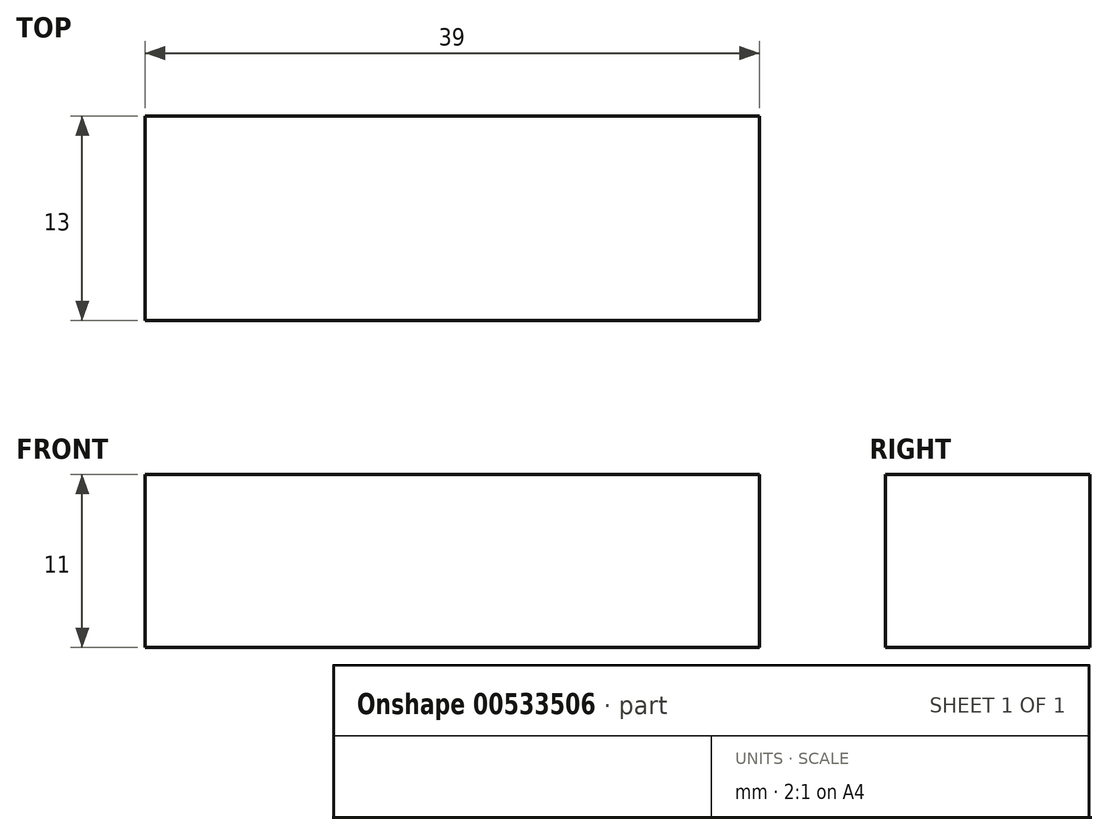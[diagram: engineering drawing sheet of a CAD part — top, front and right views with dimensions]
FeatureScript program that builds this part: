
annotation { "Feature Type Name" : "Feature", "Feature Type Description" : "" }
export const myFeature = defineFeature(function(context is Context, id is Id, definition is map)
    precondition{}
    {
        {
            var Q0;
            Q0=qCreatedBy(makeId("Top.planeOp"),FACE);
            var sketch = newSketch(context, id + "F0", { "sketchPlane" : qUnion([Q0])});
            skLineSegment(sketch, "E0.bottom", {"start": v(0, 0) * mm, "end": v(39, 0) * mm});
            skLineSegment(sketch, "E0.top", {"start": v(0, 13) * mm, "end": v(39, 13) * mm});
            skLineSegment(sketch, "E0.left", {"start": v(0, 0) * mm, "end": v(0, 13) * mm});
            skLineSegment(sketch, "E0.right", {"start": v(39, 0) * mm, "end": v(39, 13) * mm});
            skSolve(sketch);
        }
        {
            var Q0;
            Q0=qSketchRegion(id+"F0",true);
            extrude(context, id + "F1", {"entities" : qUnion([Q0]), "depth" : 11 * mm, "offsetDistance" : 25 * mm});
        }
    });
